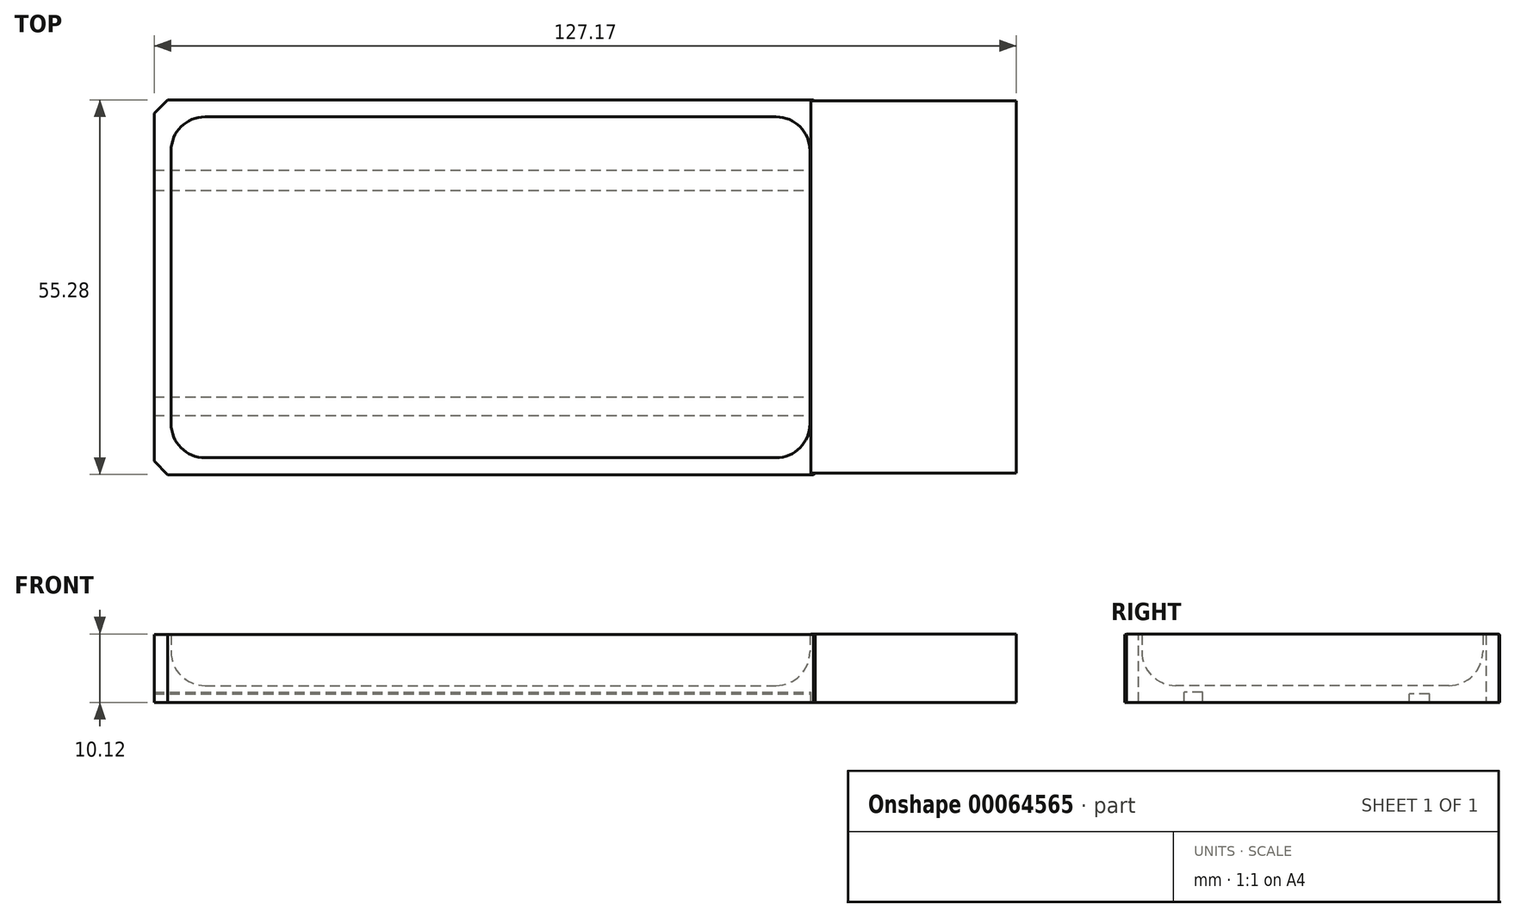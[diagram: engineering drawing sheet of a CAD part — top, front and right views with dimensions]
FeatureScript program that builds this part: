
annotation { "Feature Type Name" : "Feature", "Feature Type Description" : "" }
export const myFeature = defineFeature(function(context is Context, id is Id, definition is map)
    precondition{}
    {
        {
            var Q0;
            Q0=qCreatedBy(makeId("Top.planeOp"),FACE);
            var sketch = newSketch(context, id + "F0", { "sketchPlane" : qUnion([Q0])});
            skLineSegment(sketch, "E0.bottom", {"start": v(-43.18, 31.57) * mm, "end": v(56.04, 31.57) * mm});
            skLineSegment(sketch, "E0.top", {"start": v(-43.18, -23.71) * mm, "end": v(56.04, -23.71) * mm});
            skLineSegment(sketch, "E0.left", {"start": v(-43.18, 31.57) * mm, "end": v(-43.18, -23.71) * mm});
            skLineSegment(sketch, "E0.right", {"start": v(56.04, 31.57) * mm, "end": v(56.04, -23.71) * mm});
            skSolve(sketch);
        }
        {
            var Q0;
            Q0=makeQuery(id+"F0.imprint","IMPRINT",FACE,{"disambiguationData":[TD([[makeQuery(id+"F0.imprint","IMPRINT",EDGE,{"derivedFrom":sQuery(id+"F0.wireOp",EDGE,"3f9835f0-4a90-4386-a35f-c2b6c216ddc1")}),-1.0]])]});
            var Q1;
            Q1=makeQuery(id+"F0.imprint","IMPRINT",FACE,{"disambiguationData":[TD([[makeQuery(id+"F0.imprint","IMPRINT",EDGE,{"derivedFrom":sQuery(id+"F0.wireOp",EDGE,"E0.bottom")}),-1.0]])]});
            extrude(context, id + "F1", {"entities" : qUnion([Q0, Q1]), "depth" : 10 * mm});
        }
        {
            var Q0;
            Q0=makeQuery(id+"F1.opExtrude","CAP_FACE",FACE,{"disambiguationData":[OSD([sQuery(id+"F0.wireOp",EDGE,"E0.bottom"),sQuery(id+"F0.wireOp",EDGE,"E0.top"),sQuery(id+"F0.wireOp",EDGE,"E0.left"),sQuery(id+"F0.wireOp",EDGE,"E0.right")])],"isStart":false});
            shell(context, id + "F2", {"entities" : qUnion([Q0]), "thickness" : 2.5 * mm});
        }
        {
            var Q0;
            {var subQ0=sQuery(id+"F0.wireOp",EDGE,"E0.bottom");Q0=makeQuery(id+"F2.opShell","OFFSET_EDGE",EDGE,{"disambiguationData":[OSD([subQ0]),TDD([makeQuery(id+"F1.opExtrude","CAP_EDGE",EDGE,{"disambiguationData":[OSD([subQ0])],"isStart":true})])]});}
            var Q1;
            {var subQ0=sQuery(id+"F0.wireOp",EDGE,"E0.left");Q1=makeQuery(id+"F2.opShell","OFFSET_EDGE",EDGE,{"disambiguationData":[OSD([subQ0]),TDD([makeQuery(id+"F1.opExtrude","CAP_EDGE",EDGE,{"disambiguationData":[OSD([subQ0])],"isStart":true})])]});}
            var Q2;
            {var subQ0=sQuery(id+"F0.wireOp",EDGE,"E0.right");Q2=makeQuery(id+"F2.opShell","OFFSET_EDGE",EDGE,{"disambiguationData":[OSD([subQ0]),TDD([makeQuery(id+"F1.opExtrude","CAP_EDGE",EDGE,{"disambiguationData":[OSD([subQ0])],"isStart":true})])]});}
            var Q3;
            {var subQ0=sQuery(id+"F0.wireOp",EDGE,"E0.top");Q3=makeQuery(id+"F2.opShell","OFFSET_EDGE",EDGE,{"disambiguationData":[OSD([subQ0]),TDD([makeQuery(id+"F1.opExtrude","CAP_EDGE",EDGE,{"disambiguationData":[OSD([subQ0])],"isStart":true})])]});}
            fillet(context, id + "F3", {"entities" : qUnion([Q0, Q1, Q2, Q3]), "radius" : 5 * mm, "tangentPropagation" : true, "allowEdgeOverflow" : false});
        }
        {
            var Q0;
            {var subQ0=sQuery(id+"F0.wireOp",EDGE,"E0.right");var subQ1=sQuery(id+"F0.wireOp",EDGE,"E0.bottom");Q0=makeQuery(id+"F3.opFillet","BLEND_EDGE",EDGE,{"blendedFrom":[makeQuery(id+"F2.opShell","OFFSET_EDGE",EDGE,{"disambiguationData":[OSD([subQ1]),TDD([makeQuery(id+"F1.opExtrude","CAP_EDGE",EDGE,{"disambiguationData":[OSD([subQ1])],"isStart":true})])]}),makeQuery(id+"F2.opShell","OFFSET_EDGE",EDGE,{"disambiguationData":[OSD([subQ0]),TDD([makeQuery(id+"F1.opExtrude","CAP_EDGE",EDGE,{"disambiguationData":[OSD([subQ0])],"isStart":true})])]})],"blendedInto":[]});}
            var Q1;
            {var subQ0=sQuery(id+"F0.wireOp",EDGE,"E0.right");var subQ1=sQuery(id+"F0.wireOp",EDGE,"E0.top");Q1=makeQuery(id+"F3.opFillet","BLEND_EDGE",EDGE,{"blendedFrom":[makeQuery(id+"F2.opShell","OFFSET_EDGE",EDGE,{"disambiguationData":[OSD([subQ1]),TDD([makeQuery(id+"F1.opExtrude","CAP_EDGE",EDGE,{"disambiguationData":[OSD([subQ1])],"isStart":true})])]}),makeQuery(id+"F2.opShell","OFFSET_EDGE",EDGE,{"disambiguationData":[OSD([subQ0]),TDD([makeQuery(id+"F1.opExtrude","CAP_EDGE",EDGE,{"disambiguationData":[OSD([subQ0])],"isStart":true})])]})],"blendedInto":[]});}
            var Q2;
            {var subQ0=sQuery(id+"F0.wireOp",EDGE,"E0.left");var subQ1=sQuery(id+"F0.wireOp",EDGE,"E0.top");Q2=makeQuery(id+"F3.opFillet","BLEND_EDGE",EDGE,{"blendedFrom":[makeQuery(id+"F2.opShell","OFFSET_EDGE",EDGE,{"disambiguationData":[OSD([subQ1]),TDD([makeQuery(id+"F1.opExtrude","CAP_EDGE",EDGE,{"disambiguationData":[OSD([subQ1])],"isStart":true})])]}),makeQuery(id+"F2.opShell","OFFSET_EDGE",EDGE,{"disambiguationData":[OSD([subQ0]),TDD([makeQuery(id+"F1.opExtrude","CAP_EDGE",EDGE,{"disambiguationData":[OSD([subQ0])],"isStart":true})])]})],"blendedInto":[]});}
            var Q3;
            {var subQ0=sQuery(id+"F0.wireOp",EDGE,"E0.left");var subQ1=sQuery(id+"F0.wireOp",EDGE,"E0.bottom");Q3=makeQuery(id+"F3.opFillet","BLEND_EDGE",EDGE,{"blendedFrom":[makeQuery(id+"F2.opShell","OFFSET_EDGE",EDGE,{"disambiguationData":[OSD([subQ1]),TDD([makeQuery(id+"F1.opExtrude","CAP_EDGE",EDGE,{"disambiguationData":[OSD([subQ1])],"isStart":true})])]}),makeQuery(id+"F2.opShell","OFFSET_EDGE",EDGE,{"disambiguationData":[OSD([subQ0]),TDD([makeQuery(id+"F1.opExtrude","CAP_EDGE",EDGE,{"disambiguationData":[OSD([subQ0])],"isStart":true})])]})],"blendedInto":[]});}
            fillet(context, id + "F4", {"entities" : qUnion([Q0, Q1, Q2, Q3]), "radius" : 5 * mm, "tangentPropagation" : true, "allowEdgeOverflow" : false});
        }
        {
            var Q0;
            Q0=makeQuery(id+"F1.opExtrude","SWEPT_EDGE",EDGE,{"disambiguationData":[OSD([sQuery(id+"F0.wireOp",EDGE,"E0.top"),sQuery(id+"F0.wireOp",EDGE,"E0.right")])]});
            var Q1;
            Q1=makeQuery(id+"F1.opExtrude","SWEPT_EDGE",EDGE,{"disambiguationData":[OSD([sQuery(id+"F0.wireOp",EDGE,"E0.bottom"),sQuery(id+"F0.wireOp",EDGE,"E0.right")])]});
            var Q2;
            Q2=makeQuery(id+"F1.opExtrude","SWEPT_EDGE",EDGE,{"disambiguationData":[OSD([sQuery(id+"F0.wireOp",EDGE,"E0.top"),sQuery(id+"F0.wireOp",EDGE,"E0.left")])]});
            var Q3;
            Q3=makeQuery(id+"F1.opExtrude","SWEPT_EDGE",EDGE,{"disambiguationData":[OSD([sQuery(id+"F0.wireOp",EDGE,"E0.bottom"),sQuery(id+"F0.wireOp",EDGE,"E0.left")])]});
            chamfer(context, id + "F5", {"entities" : qUnion([Q0, Q1, Q2, Q3]), "width" : 2 * mm, "tangentPropagation" : true});
        }
        {
            var Q0;
            Q0=qCreatedBy(makeId("Right.planeOp"),FACE);
            var sketch = newSketch(context, id + "F6", { "sketchPlane" : qUnion([Q0])});
            skLineSegment(sketch, "E1.bottom", {"start": v(-14.98, 1.5) * mm, "end": v(-12.23, 1.5) * mm});
            skLineSegment(sketch, "E1.top", {"start": v(-14.98, -1.75) * mm, "end": v(-12.23, -1.75) * mm});
            skLineSegment(sketch, "E1.left", {"start": v(-14.98, 1.5) * mm, "end": v(-14.98, -1.75) * mm});
            skLineSegment(sketch, "E1.right", {"start": v(-12.23, 1.5) * mm, "end": v(-12.23, -1.75) * mm});
            skLineSegment(sketch, "E2.bottom", {"start": v(18.22, 1.25) * mm, "end": v(21.22, 1.25) * mm});
            skLineSegment(sketch, "E2.top", {"start": v(18.22, -1.87) * mm, "end": v(21.22, -1.87) * mm});
            skLineSegment(sketch, "E2.left", {"start": v(18.22, 1.25) * mm, "end": v(18.22, -1.87) * mm});
            skLineSegment(sketch, "E2.right", {"start": v(21.22, 1.25) * mm, "end": v(21.22, -1.87) * mm});
            skSolve(sketch);
        }
        {
            var Q0;
            Q0 = qSketchRegion(id + "F6", true);
            extrude(context, id + "F7", {"entities" : qUnion([Q0]), "operationType" : NewBodyOperationType.REMOVE, "endBound" : BoundingType.SYMMETRIC, "oppositeDirection" : true, "depth" : 117.62 * mm});
        }
        {
            var Q0;
            Q0=qCreatedBy(makeId("Top.planeOp"),FACE);
            var sketch = newSketch(context, id + "F8", { "sketchPlane" : qUnion([Q0])});
            skLineSegment(sketch, "E3.bottom", {"start": v(53.66, 31.45) * mm, "end": v(84, 31.45) * mm});
            skLineSegment(sketch, "E3.top", {"start": v(53.66, -23.46) * mm, "end": v(84, -23.46) * mm});
            skLineSegment(sketch, "E3.left", {"start": v(53.66, 31.45) * mm, "end": v(53.66, -23.46) * mm});
            skLineSegment(sketch, "E3.right", {"start": v(84, 31.45) * mm, "end": v(84, -23.46) * mm});
            skSolve(sketch);
        }
        {
            var Q0;
            Q0=makeQuery(id+"F8.imprint","IMPRINT",FACE,{"disambiguationData":[TD([[makeQuery(id+"F8.imprint","IMPRINT",EDGE,{"derivedFrom":sQuery(id+"F8.wireOp",EDGE,"E3.bottom")}),-1.0]])]});
            extrude(context, id + "F9", {"entities" : qUnion([Q0]), "operationType" : NewBodyOperationType.ADD, "depth" : 10.12 * mm});
        }
    });
